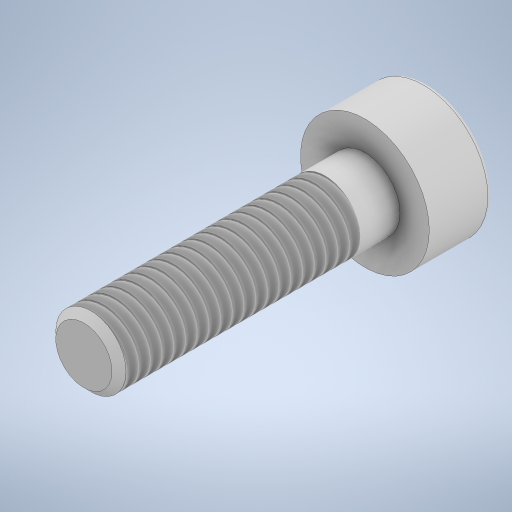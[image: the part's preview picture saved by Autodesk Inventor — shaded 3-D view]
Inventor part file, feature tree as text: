
AUTODESK INVENTOR PART (.ipt)
format: ipt  version: 2024 (Build 280153000, 153)  size: 294,912 bytes
history: native  units: in
note: dims shown in document units (in); Inventor stores cm internally (conversion verified against a paired STEP export)
features: extrude x3, sketch x2, plane x1, chamfer x1, fillet x1, thread x1
ambient origin geometry x8: Origin, YZ Plane, XZ Plane, XY Plane, X Axis, Y Axis, Z Axis, Center Point
bodies: Solid1 (feature_tree)
feature tree (9):
  sketch  "Sketch1"  dims[d0=0.2165in d1=0.1137in]
  extrude  "Extrusion1"  Depth=0.1137in
  extrude  "Extrusion2"  Depth=0.0492in TaperAngle=0.0deg
  plane  "Work Plane1"
  extrude  "Extrusion3"  TaperAngle=0.0deg  [1 undecoded]
  chamfer  "Chamfer1"  Distance=0.1181in
  fillet  "Fillet1"  Radius=0.4724in
  thread  "Thread1"  [1 undecoded]
  sketch  "Sketch2"  dims[d2=0.1063in d3=0.0in d4=0.0492in d5=0.0in d6=0.0in d7=0.1181in d8=0.4724in d9=0.0in d10=0.0118in d11=0.0787in d12=45.0deg d13=0.0079in d14=0.3937in d15=0.0in]
note: 2 required parameter values undecoded (feature->parameter linkage not recoverable at this tier; creation-order binding heuristic only, values carry confidence <= 0.55)
